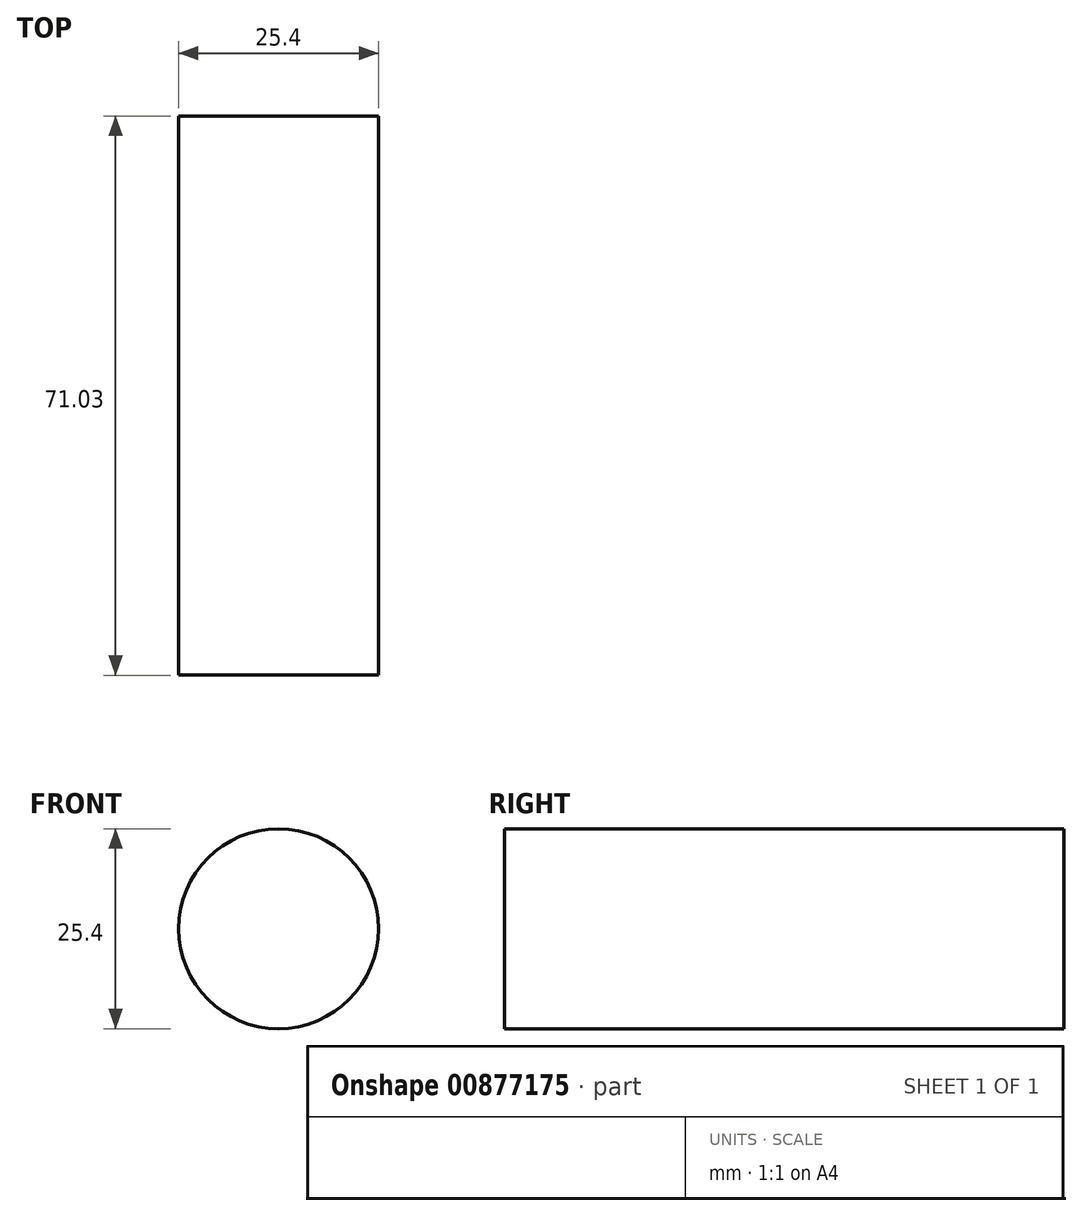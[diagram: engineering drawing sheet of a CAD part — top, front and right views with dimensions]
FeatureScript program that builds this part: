
annotation { "Feature Type Name" : "Feature", "Feature Type Description" : "" }
export const myFeature = defineFeature(function(context is Context, id is Id, definition is map)
    precondition{}
    {
        {
            var Q0;
            Q0=qCreatedBy(makeId("Front.planeOp"),FACE);
            var sketch = newSketch(context, id + "F0", { "sketchPlane" : qUnion([Q0])});
            skCircle(sketch, "E0", {"center": v(0, 0) * mm, "radius": 12.7 * mm});
            skSolve(sketch);
        }
        {
            var Q0;
            Q0 = qSketchRegion(id + "F0", true);
            extrude(context, id + "F1", {"entities" : qUnion([Q0]), "depth" : 71.03 * mm, "offsetDistance" : 25 * mm});
        }
    });
